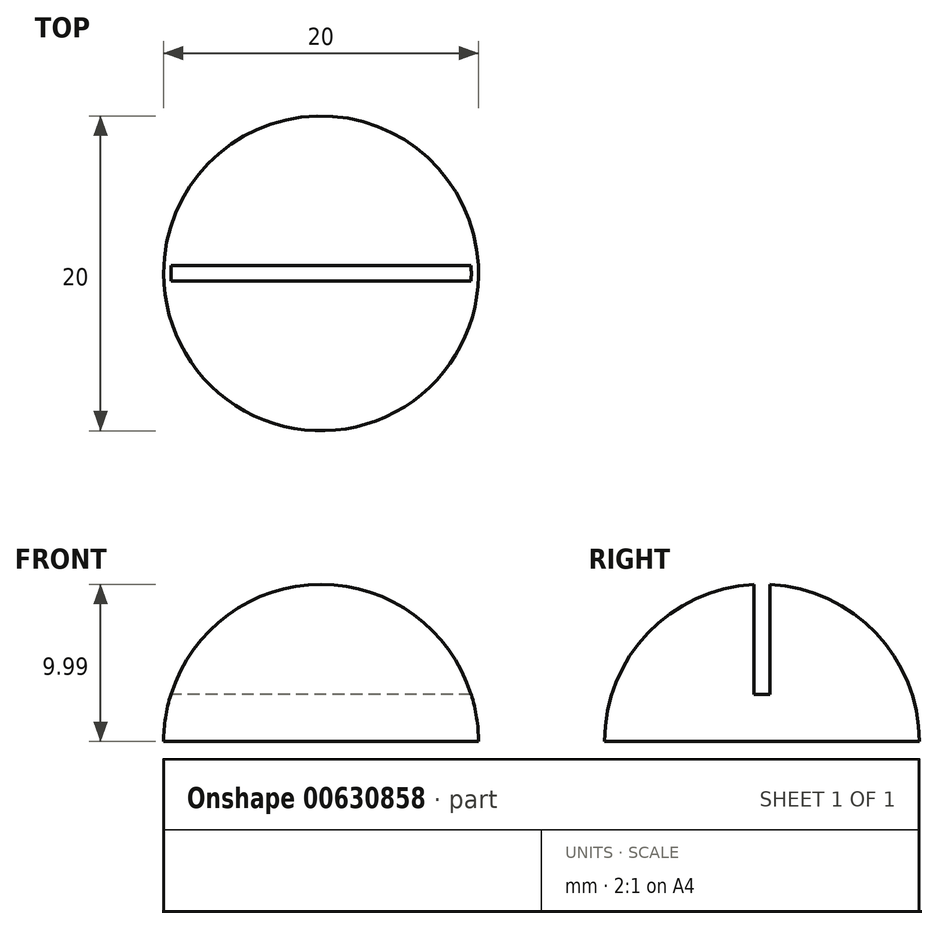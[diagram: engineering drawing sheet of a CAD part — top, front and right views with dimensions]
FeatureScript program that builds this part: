
annotation { "Feature Type Name" : "Feature", "Feature Type Description" : "" }
export const myFeature = defineFeature(function(context is Context, id is Id, definition is map)
    precondition{}
    {
        {
            var Q0;
            Q0=qCreatedBy(makeId("Front.planeOp"),FACE);
            var sketch = newSketch(context, id + "F0", { "sketchPlane" : qUnion([Q0])});
            skArc(sketch, "E0", {"start": v(10, 0) * mm, "mid": v(7.07, 7.07) * mm, "end": v(0, 10) * mm});
            skLineSegment(sketch, "E1", {"start": v(0, 0) * mm, "end": v(10, 0) * mm});
            skLineSegment(sketch, "E2", {"start": v(0, 0) * mm, "end": v(0, 10) * mm});
            skSolve(sketch);
        }
        {
            var Q0;
            Q0=makeQuery(id+"F0.imprint","IMPRINT",FACE,{"disambiguationData":[TD([[makeQuery(id+"F0.imprint","IMPRINT",EDGE,{"derivedFrom":sQuery(id+"F0.wireOp",EDGE,"E0")}),1.0]])]});
            var Q1;
            Q1=sQuery(id+"F0.wireOp",EDGE,"E2");
            revolve(context, id + "F1", {"entities" : qUnion([Q0]), "axis" : qUnion([Q1]), "revolveType" : RevolveType.FULL});
        }
        {
            var Q0;
            Q0=qCreatedBy(makeId("Top.planeOp"),FACE);
            cPlane(context, id + "F2", {"entities" : qUnion([Q0]), "cplaneType" : CPlaneType.OFFSET, "offset" : 15 * mm, "width" : 150 * mm, "height" : 150 * mm});
        }
        {
            var Q0;
            Q0=qCreatedBy(id+"F2.planeOp",FACE);
            var sketch = newSketch(context, id + "F3", { "sketchPlane" : qUnion([Q0])});
            skLineSegment(sketch, "E3.bottom", {"start": v(12.5, -0.5) * mm, "end": v(-12.5, -0.5) * mm});
            skLineSegment(sketch, "E3.top", {"start": v(12.5, 0.5) * mm, "end": v(-12.5, 0.5) * mm});
            skLineSegment(sketch, "E3.left", {"start": v(12.5, -0.5) * mm, "end": v(12.5, 0.5) * mm});
            skLineSegment(sketch, "E3.right", {"start": v(-12.5, -0.5) * mm, "end": v(-12.5, 0.5) * mm});
            skPoint(sketch, "E3.middle", {"position": v(0, 0) * mm});
            skSolve(sketch);
        }
        {
            var Q0;
            Q0=makeQuery(id+"F3.imprint","IMPRINT",FACE,{"disambiguationData":[TD([[makeQuery(id+"F3.imprint","IMPRINT",EDGE,{"derivedFrom":sQuery(id+"F3.wireOp",EDGE,"E3.bottom")}),-1.0]])]});
            extrude(context, id + "F4", {"entities" : qUnion([Q0]), "operationType" : NewBodyOperationType.REMOVE, "oppositeDirection" : true, "depth" : 12 * mm, "offsetDistance" : 25 * mm});
        }
    });
